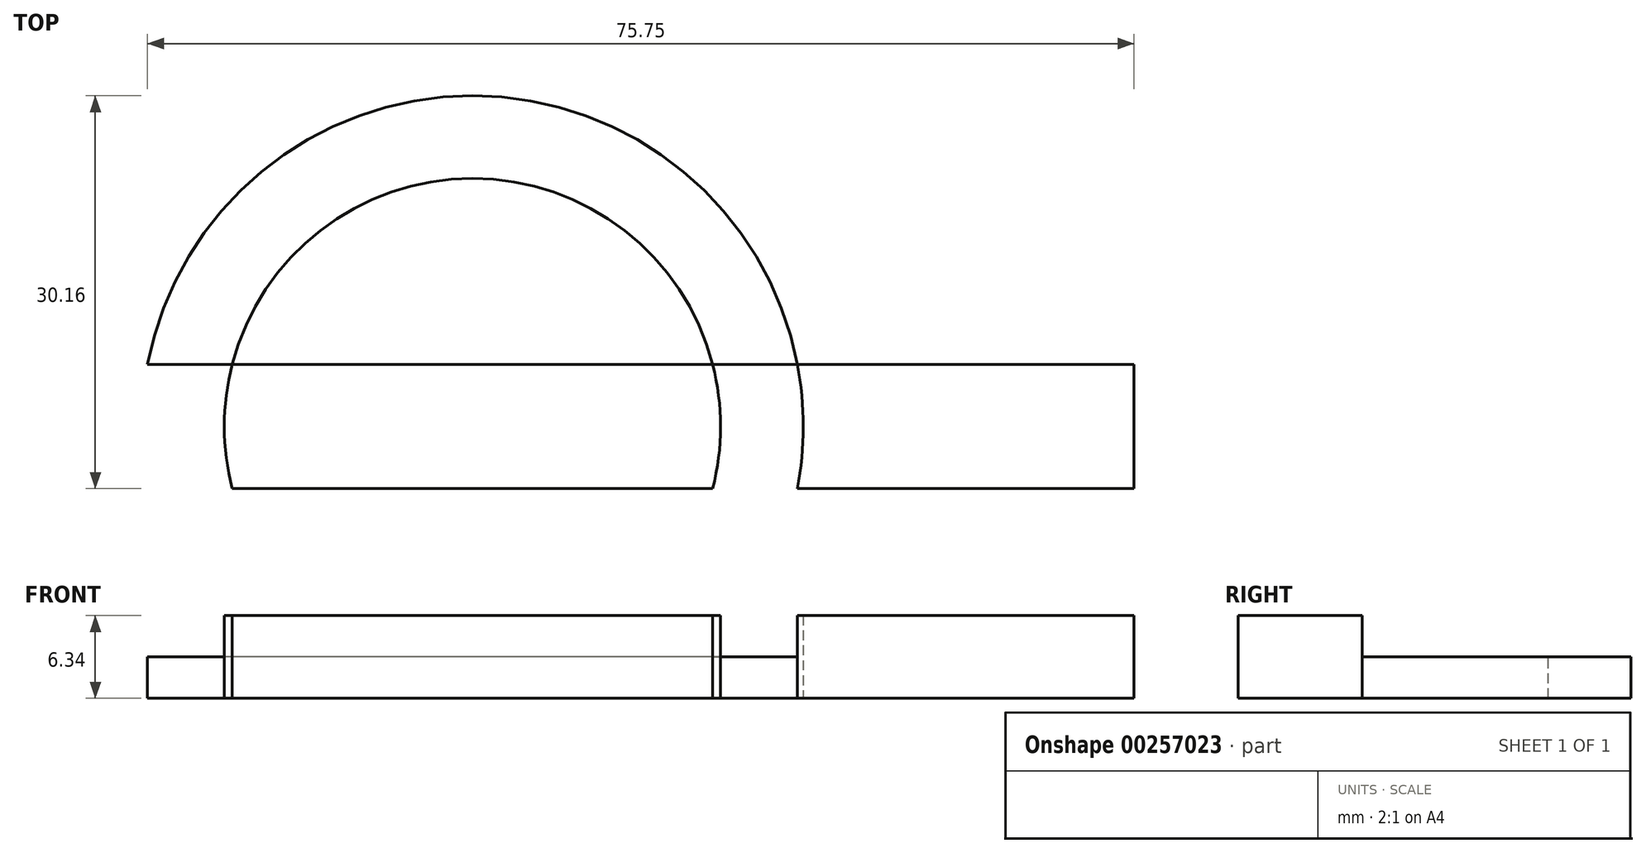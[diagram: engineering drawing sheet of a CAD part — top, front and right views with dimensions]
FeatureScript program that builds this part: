
annotation { "Feature Type Name" : "Feature", "Feature Type Description" : "" }
export const myFeature = defineFeature(function(context is Context, id is Id, definition is map)
    precondition{}
    {
        {
            var Q0;
            Q0=qCreatedBy(makeId("Top.planeOp"),FACE);
            var sketch = newSketch(context, id + "F0", { "sketchPlane" : qUnion([Q0])});
            skCircle(sketch, "E0", {"center": v(0, 0) * mm, "radius": 19.05 * mm});
            skLineSegment(sketch, "E1.bottom", {"start": v(18.45, 4.76) * mm, "end": v(-18.45, 4.76) * mm});
            skLineSegment(sketch, "E1.top", {"start": v(18.45, -4.76) * mm, "end": v(-18.45, -4.76) * mm});
            skLineSegment(sketch, "E1.left", {"start": v(18.45, 4.76) * mm, "end": v(18.45, -4.76) * mm});
            skLineSegment(sketch, "E1.right", {"start": v(-18.45, 4.76) * mm, "end": v(-18.45, -4.76) * mm});
            skLineSegment(sketch, "E2.bottom", {"start": v(50.8, 25.4) * mm, "end": v(-50.8, 25.4) * mm});
            skLineSegment(sketch, "E2.top", {"start": v(50.8, -25.4) * mm, "end": v(-50.8, -25.4) * mm});
            skLineSegment(sketch, "E2.left", {"start": v(50.8, 25.4) * mm, "end": v(50.8, -25.4) * mm});
            skLineSegment(sketch, "E2.right", {"start": v(-50.8, 25.4) * mm, "end": v(-50.8, -25.4) * mm});
            skLineSegment(sketch, "E3.bottom", {"start": v(-18.45, 4.76) * mm, "end": v(-50.8, 4.76) * mm});
            skLineSegment(sketch, "E3.top", {"start": v(-18.45, -4.76) * mm, "end": v(-50.8, -4.76) * mm});
            skLineSegment(sketch, "E3.right", {"start": v(-50.8, 4.76) * mm, "end": v(-50.8, -4.76) * mm});
            skLineSegment(sketch, "E4.bottom", {"start": v(-50.8, 4.76) * mm, "end": v(50.8, 4.76) * mm});
            skLineSegment(sketch, "E4.top", {"start": v(-50.8, -4.76) * mm, "end": v(50.8, -4.76) * mm});
            skLineSegment(sketch, "E4.right", {"start": v(50.8, 4.76) * mm, "end": v(50.8, -4.76) * mm});
            skLineSegment(sketch, "E5", {"start": v(-25.4, 4.76) * mm, "end": v(-25.4, -4.76) * mm});
            skCircle(sketch, "E6", {"center": v(0, 0) * mm, "radius": 25.4 * mm});
            skSolve(sketch);
        }
        {
            var Q0;
            {var subQ4=sQuery(id+"F0.wireOp",EDGE,"E3.right");Q0=makeQuery(id+"F0.imprint","IMPRINT",FACE,{"disambiguationData":[TD([[makeQuery(id+"F0.imprint","IMPRINT",EDGE,{"derivedFrom":subQ4}),1.0]])]});}
            var Q1;
            {var subQ0=sQuery(id+"F0.wireOp",EDGE,"E1.right");Q1=makeQuery(id+"F0.imprint","IMPRINT",FACE,{"disambiguationData":[TD([[makeQuery(id+"F0.imprint","IMPRINT",EDGE,{"derivedFrom":subQ0}),-1.0]])]});}
            var Q2;
            {var subQ0=sQuery(id+"F0.wireOp",EDGE,"E1.left");Q2=makeQuery(id+"F0.imprint","IMPRINT",FACE,{"disambiguationData":[TD([[makeQuery(id+"F0.imprint","IMPRINT",EDGE,{"derivedFrom":subQ0}),-1.0]])]});}
            var Q3;
            {var subQ0=sQuery(id+"F0.wireOp",EDGE,"E1.left");Q3=makeQuery(id+"F0.imprint","IMPRINT",FACE,{"disambiguationData":[TD([[makeQuery(id+"F0.imprint","IMPRINT",EDGE,{"derivedFrom":subQ0}),1.0]])]});}
            var Q4;
            {var subQ0=sQuery(id+"F0.wireOp",EDGE,"E5");var subQ1=sQuery(id+"F0.wireOp",EDGE,"E4.top");var subQ2=makeQuery(id+"F0.imprint","INTERSECT",VERTEX,{"derivedFrom":[subQ1,subQ0]});Q4=makeQuery(id+"F0.imprint","IMPRINT",FACE,{"disambiguationData":[TD([[makeQuery(id+"F0.imprint","IMPRINT",EDGE,{"disambiguationData":[TD([[subQ2,-1.0]])],"derivedFrom":subQ1}),1.0]])]});}
            var Q5;
            {var subQ0=sQuery(id+"F0.wireOp",EDGE,"E5");var subQ1=sQuery(id+"F0.wireOp",EDGE,"E4.bottom");var subQ2=makeQuery(id+"F0.imprint","INTERSECT",VERTEX,{"derivedFrom":[subQ1,subQ0]});Q5=makeQuery(id+"F0.imprint","IMPRINT",FACE,{"disambiguationData":[TD([[makeQuery(id+"F0.imprint","IMPRINT",EDGE,{"disambiguationData":[TD([[subQ2,-1.0]])],"derivedFrom":subQ1}),-1.0]])]});}
            extrude(context, id + "F1", {"entities" : qUnion([Q0, Q1, Q2, Q3, Q4, Q5]), "depth" : 3.17 * mm});
        }
        {
            var Q0;
            {var subQ0=sQuery(id+"F0.wireOp",EDGE,"E6");var subQ1=sQuery(id+"F0.wireOp",EDGE,"E4.bottom");var subQ2=makeQuery(id+"F0.imprint","INTERSECT",VERTEX,{"disambiguationData":[OD(0.0)],"derivedFrom":[subQ1,subQ0]});Q0=makeQuery(id+"F0.imprint","IMPRINT",FACE,{"disambiguationData":[TD([[makeQuery(id+"F0.imprint","IMPRINT",EDGE,{"disambiguationData":[TD([[subQ2,-1.0]])],"derivedFrom":subQ0}),1.0]])]});}
            var Q1;
            {var subQ0=sQuery(id+"F0.wireOp",EDGE,"E5");var subQ1=sQuery(id+"F0.wireOp",EDGE,"E4.bottom");var subQ2=makeQuery(id+"F0.imprint","INTERSECT",VERTEX,{"derivedFrom":[subQ1,subQ0]});Q1=makeQuery(id+"F0.imprint","IMPRINT",FACE,{"disambiguationData":[TD([[makeQuery(id+"F0.imprint","IMPRINT",EDGE,{"disambiguationData":[TD([[subQ2,-1.0]])],"derivedFrom":subQ1}),-1.0]])]});}
            var Q2;
            {var subQ4=sQuery(id+"F0.wireOp",EDGE,"E3.right");Q2=makeQuery(id+"F0.imprint","IMPRINT",FACE,{"disambiguationData":[TD([[makeQuery(id+"F0.imprint","IMPRINT",EDGE,{"derivedFrom":subQ4}),1.0]])]});}
            var Q3;
            {var subQ0=sQuery(id+"F0.wireOp",EDGE,"E5");var subQ1=sQuery(id+"F0.wireOp",EDGE,"E4.top");var subQ2=makeQuery(id+"F0.imprint","INTERSECT",VERTEX,{"derivedFrom":[subQ1,subQ0]});Q3=makeQuery(id+"F0.imprint","IMPRINT",FACE,{"disambiguationData":[TD([[makeQuery(id+"F0.imprint","IMPRINT",EDGE,{"disambiguationData":[TD([[subQ2,-1.0]])],"derivedFrom":subQ1}),1.0]])]});}
            var Q4;
            {var subQ0=sQuery(id+"F0.wireOp",EDGE,"E1.right");Q4=makeQuery(id+"F0.imprint","IMPRINT",FACE,{"disambiguationData":[TD([[makeQuery(id+"F0.imprint","IMPRINT",EDGE,{"derivedFrom":subQ0}),-1.0]])]});}
            var Q5;
            {var subQ0=sQuery(id+"F0.wireOp",EDGE,"E1.left");Q5=makeQuery(id+"F0.imprint","IMPRINT",FACE,{"disambiguationData":[TD([[makeQuery(id+"F0.imprint","IMPRINT",EDGE,{"derivedFrom":subQ0}),-1.0]])]});}
            var Q6;
            {var subQ0=sQuery(id+"F0.wireOp",EDGE,"E1.left");Q6=makeQuery(id+"F0.imprint","IMPRINT",FACE,{"disambiguationData":[TD([[makeQuery(id+"F0.imprint","IMPRINT",EDGE,{"derivedFrom":subQ0}),1.0]])]});}
            extrude(context, id + "F2", {"entities" : qUnion([Q0, Q1, Q2, Q3, Q4, Q5, Q6]), "operationType" : NewBodyOperationType.ADD, "oppositeDirection" : true, "depth" : 3.17 * mm});
        }
    });
